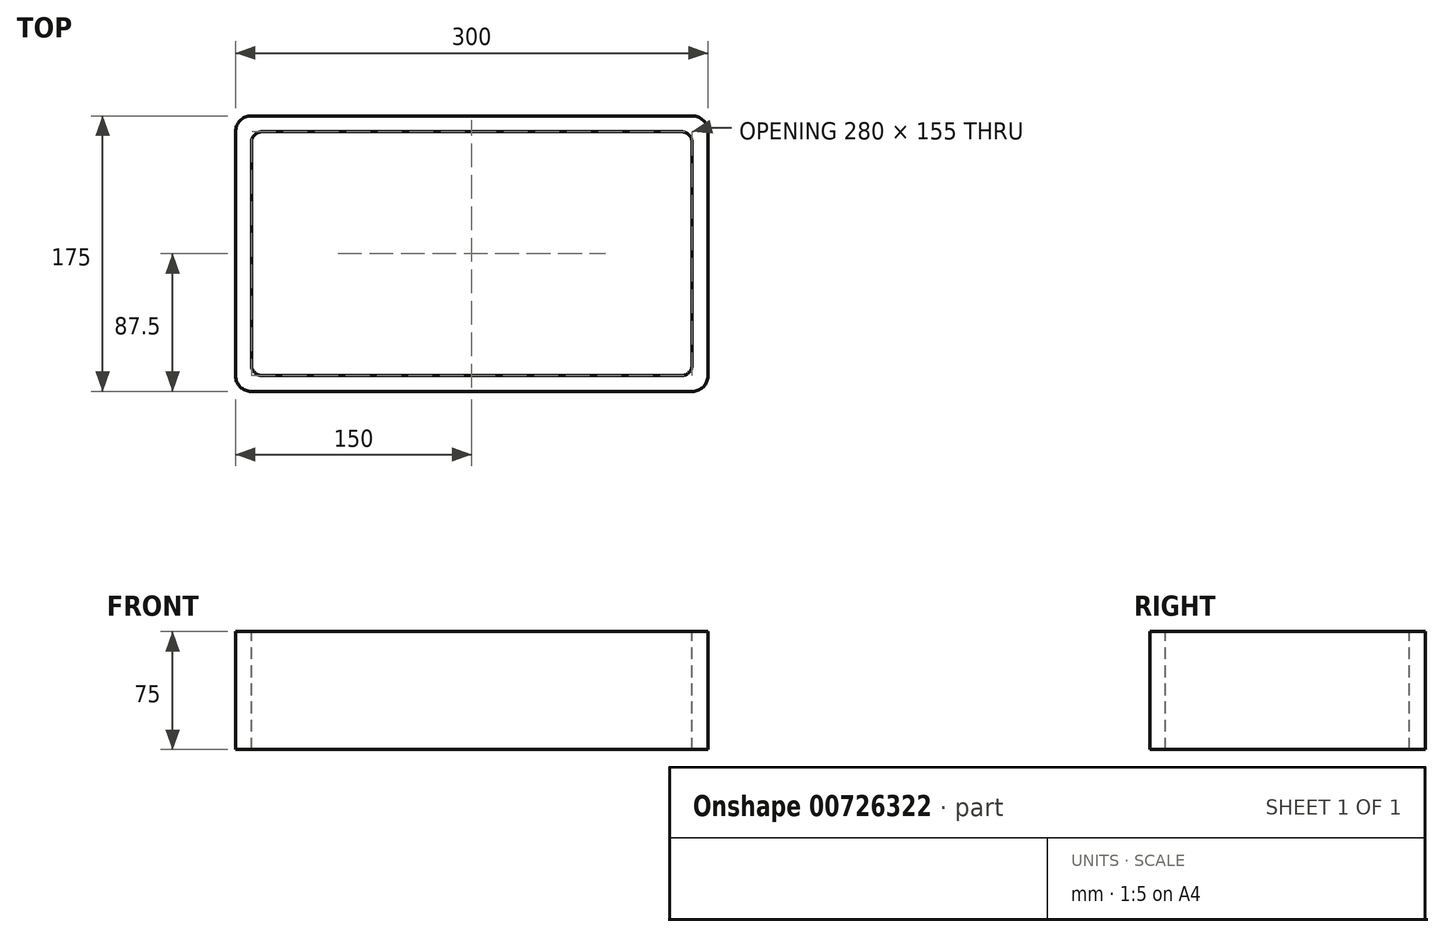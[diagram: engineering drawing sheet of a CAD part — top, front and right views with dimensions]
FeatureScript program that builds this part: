
annotation { "Feature Type Name" : "Feature", "Feature Type Description" : "" }
export const myFeature = defineFeature(function(context is Context, id is Id, definition is map)
    precondition{}
    {
        {
            var Q0;
            Q0=qCreatedBy(makeId("Top.planeOp"),FACE);
            var sketch = newSketch(context, id + "F0", { "sketchPlane" : qUnion([Q0])});
            skLineSegment(sketch, "E0.bottom", {"start": v(-140, 87.5) * mm, "end": v(140, 87.5) * mm});
            skLineSegment(sketch, "E0.top", {"start": v(-140, -87.5) * mm, "end": v(140, -87.5) * mm});
            skLineSegment(sketch, "E0.left", {"start": v(-150, 77.5) * mm, "end": v(-150, -77.5) * mm});
            skLineSegment(sketch, "E0.right", {"start": v(150, 77.5) * mm, "end": v(150, -77.5) * mm});
            skPoint(sketch, "E0.middle", {"position": v(0, 0) * mm});
            skPoint(sketch, "E1.visualSharp", {"position": v(-150, 87.5) * mm});
            skArc(sketch, "E1.filletArc", {"start": v(-140, 87.5) * mm, "mid": v(-147.07, 84.57) * mm, "end": v(-150, 77.5) * mm});
            skPoint(sketch, "E2.visualSharp", {"position": v(-150, -87.5) * mm});
            skArc(sketch, "E2.filletArc", {"start": v(-150, -77.5) * mm, "mid": v(-147.07, -84.57) * mm, "end": v(-140, -87.5) * mm});
            skPoint(sketch, "E3.visualSharp", {"position": v(150, -87.5) * mm});
            skArc(sketch, "E3.filletArc", {"start": v(140, -87.5) * mm, "mid": v(147.07, -84.57) * mm, "end": v(150, -77.5) * mm});
            skPoint(sketch, "E4.visualSharp", {"position": v(150, 87.5) * mm});
            skArc(sketch, "E4.filletArc", {"start": v(150, 77.5) * mm, "mid": v(147.07, 84.57) * mm, "end": v(140, 87.5) * mm});
            skLineSegment(sketch, "E5.bottom", {"start": v(-133, 77.5) * mm, "end": v(133, 77.5) * mm});
            skLineSegment(sketch, "E5.top", {"start": v(-133, -77.5) * mm, "end": v(133, -77.5) * mm});
            skLineSegment(sketch, "E5.left", {"start": v(-140, 70.5) * mm, "end": v(-140, -70.5) * mm});
            skLineSegment(sketch, "E5.right", {"start": v(140, 70.5) * mm, "end": v(140, -70.5) * mm});
            skArc(sketch, "E6.filletArc", {"start": v(-133, 77.5) * mm, "mid": v(-137.95, 75.45) * mm, "end": v(-140, 70.5) * mm});
            skArc(sketch, "E7.filletArc", {"start": v(140, 70.5) * mm, "mid": v(137.95, 75.45) * mm, "end": v(133, 77.5) * mm});
            skArc(sketch, "E8.filletArc", {"start": v(-140, -70.5) * mm, "mid": v(-137.95, -75.45) * mm, "end": v(-133, -77.5) * mm});
            skArc(sketch, "E9.filletArc", {"start": v(133, -77.5) * mm, "mid": v(137.95, -75.45) * mm, "end": v(140, -70.5) * mm});
            skSolve(sketch);
        }
        {
            var Q0;
            Q0 = qSketchRegion(id + "F0", true);
            extrude(context, id + "F1", {"entities" : qUnion([Q0]), "oppositeDirection" : true, "depth" : 75 * mm, "offsetDistance" : 25 * mm});
        }
    });
